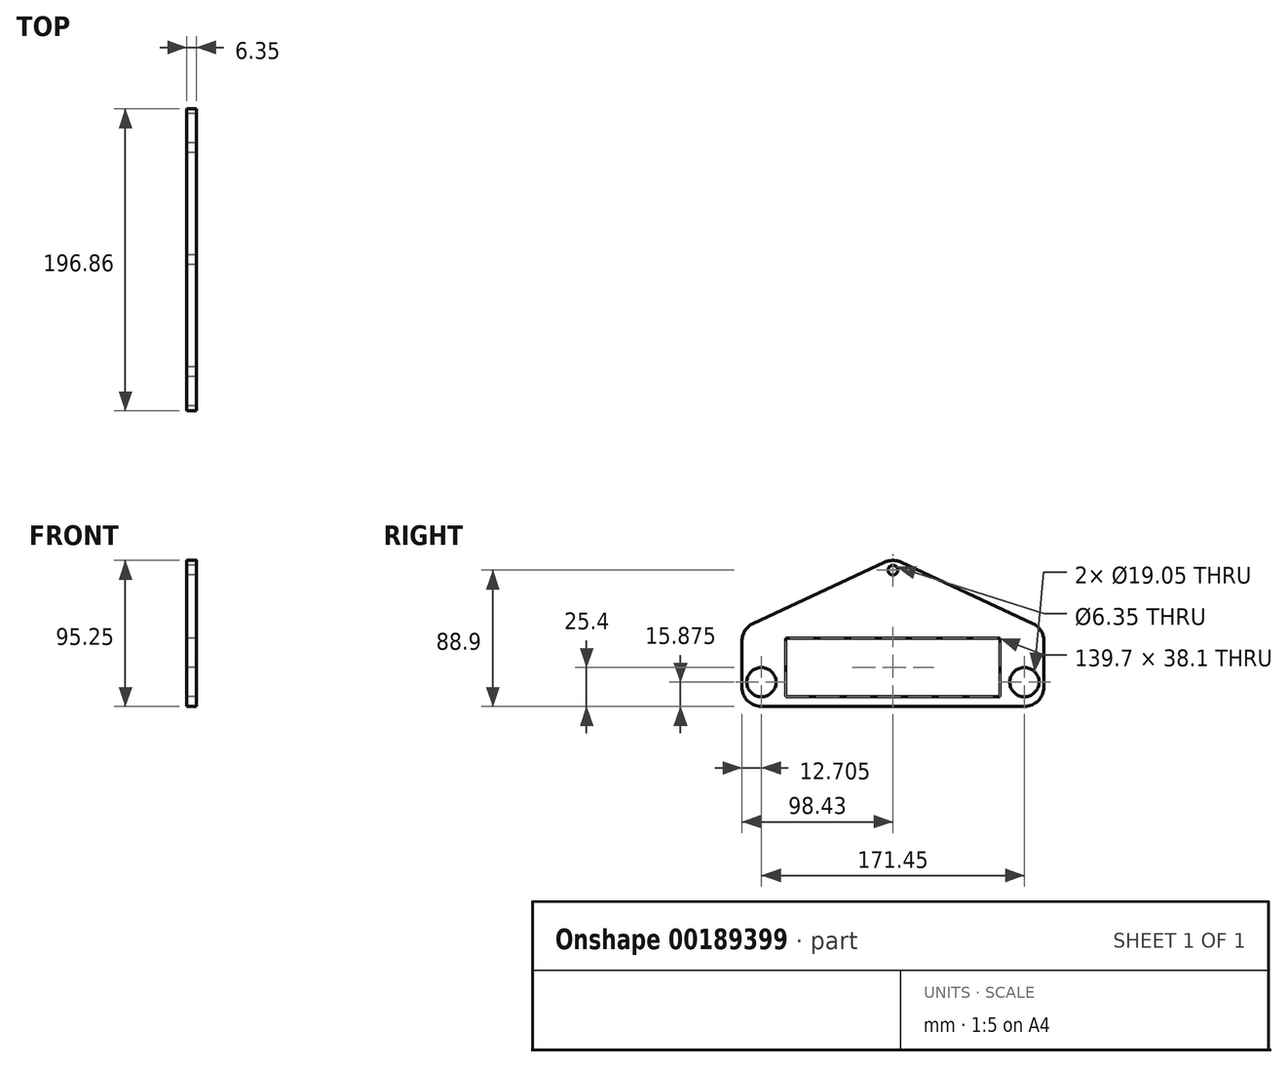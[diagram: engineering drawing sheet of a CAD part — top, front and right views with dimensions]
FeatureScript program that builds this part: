
annotation { "Feature Type Name" : "Feature", "Feature Type Description" : "" }
export const myFeature = defineFeature(function(context is Context, id is Id, definition is map)
    precondition{}
    {
        {
            var Q0;
            Q0=qCreatedBy(makeId("Right.planeOp"),FACE);
            var sketch = newSketch(context, id + "F0", { "sketchPlane" : qUnion([Q0])});
            skLineSegment(sketch, "E0.bottom", {"start": v(85.73, -25.4) * mm, "end": v(-85.72, -25.4) * mm});
            skLineSegment(sketch, "E0.left", {"start": v(98.43, -12.7) * mm, "end": v(98.42, 17.3) * mm});
            skLineSegment(sketch, "E0.right", {"start": v(-98.42, -12.7) * mm, "end": v(-98.43, 17.3) * mm});
            skPoint(sketch, "E0.middle", {"position": v(0, 0) * mm});
            skCircle(sketch, "E1", {"center": v(85.73, -9.53) * mm, "radius": 9.53 * mm});
            skCircle(sketch, "E2", {"center": v(-85.72, -9.53) * mm, "radius": 9.53 * mm});
            skLineSegment(sketch, "E3.bottom", {"start": v(69.85, -19.05) * mm, "end": v(-69.85, -19.05) * mm});
            skLineSegment(sketch, "E3.top", {"start": v(69.85, 19.05) * mm, "end": v(-69.85, 19.05) * mm});
            skLineSegment(sketch, "E3.left", {"start": v(69.85, -19.05) * mm, "end": v(69.85, 19.05) * mm});
            skLineSegment(sketch, "E3.right", {"start": v(-69.85, -19.05) * mm, "end": v(-69.85, 19.05) * mm});
            skLineSegment(sketch, "E4", {"start": v(85.73, -9.53) * mm, "end": v(98.43, -9.53) * mm, "construction": true});
            skLineSegment(sketch, "E5", {"start": v(-85.72, -9.53) * mm, "end": v(-98.42, -9.53) * mm, "construction": true});
            skLineSegment(sketch, "E6", {"start": v(-91.08, 28.82) * mm, "end": v(-5.35, 68.67) * mm});
            skLineSegment(sketch, "E7", {"start": v(5.35, 68.67) * mm, "end": v(91.08, 28.82) * mm});
            skCircle(sketch, "E8", {"center": v(0, 63.5) * mm, "radius": 3.18 * mm});
            skPoint(sketch, "E9.visualSharp", {"position": v(-98.42, -25.4) * mm});
            skArc(sketch, "E9.filletArc", {"start": v(-98.42, -12.7) * mm, "mid": v(-94.7, -21.68) * mm, "end": v(-85.72, -25.4) * mm});
            skPoint(sketch, "E10.visualSharp", {"position": v(-98.43, 25.4) * mm});
            skArc(sketch, "E10.filletArc", {"start": v(-91.08, 28.82) * mm, "mid": v(-96.43, 24.13) * mm, "end": v(-98.43, 17.3) * mm});
            skPoint(sketch, "E11.visualSharp", {"position": v(0, 71.16) * mm});
            skArc(sketch, "E11.filletArc", {"start": v(5.35, 68.67) * mm, "mid": v(0, 69.85) * mm, "end": v(-5.35, 68.67) * mm});
            skPoint(sketch, "E12.visualSharp", {"position": v(98.42, 25.4) * mm});
            skArc(sketch, "E12.filletArc", {"start": v(98.42, 17.3) * mm, "mid": v(96.43, 24.13) * mm, "end": v(91.08, 28.82) * mm});
            skPoint(sketch, "E13.visualSharp", {"position": v(98.43, -25.4) * mm});
            skArc(sketch, "E13.filletArc", {"start": v(85.73, -25.4) * mm, "mid": v(94.7, -21.68) * mm, "end": v(98.43, -12.7) * mm});
            skSolve(sketch);
        }
        {
            var Q0;
            Q0 = qSketchRegion(id + "F0", true);
            extrude(context, id + "F1", {"entities" : qUnion([Q0]), "depth" : 6.35 * mm});
        }
    });
